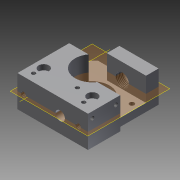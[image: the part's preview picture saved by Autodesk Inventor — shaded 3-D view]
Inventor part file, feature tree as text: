
AUTODESK INVENTOR PART (.ipt)
format: ipt  version: 2015 (Build 190159000, 159)  size: 257,536 bytes
history: native  units: mm
features: hole x11, extrude x4, projected_geometry x3, other x2, chamfer x1, plane x1, sketch x1
ambient origin geometry x8: Origin, YZ Plane, XZ Plane, XY Plane, X Axis, Y Axis, Z Axis, Center Point
bodies: Solid1 (feature_tree)
feature tree (23):
  extrude  "Extrusión1"  Depth=10.0mm
  hole  "Agujero1"  [1 undecoded]
  extrude  "Extrusión2"  Depth=10.0mm
  hole  "Agujero2"  [1 undecoded]
  hole  "Agujero3"  [1 undecoded]
  hole  "Agujero4"  [1 undecoded]
  hole  "Agujero5"  [1 undecoded]
  hole  "Agujero10"  [1 undecoded]
  hole  "Agujero11"  [1 undecoded]
  other  "Desplazar cara3"
  other  "Eje de trabajo1"
  hole  "Agujero13"  [1 undecoded]
  extrude  "Extrusión9"  Depth=10.0mm
  extrude  "Extrusión10"  Depth=10.0mm
  chamfer  "Chaflán4"  Distance=32.0mm
  hole  "Agujero14"  [1 undecoded]
  plane  "Plano de trabajo2"
  hole  "Agujero15"  [1 undecoded]
  hole  "Agujero16"  [1 undecoded]
  sketch  "Boceto15"  dims[d0=42.5mm d1=49.0mm d2=22.0mm d3=26.5mm d4=31.0mm d5=3.5mm d6=20.0mm d7=0.0mm d8=35.0mm d9=3.242mm d10=6.0mm d11=4.0mm d12=2.0mm d13=90.0deg d14=8.0mm d15=20.594885mm d17=13.0mm d19=15.0mm d20=0.0mm d22=6.0mm d23=6.0mm d24=6.0mm d25=4.0mm d26=2.0mm d27=90.0deg d28=20.0mm d29=20.594885mm d37=5.0mm d38=15.0mm d39=6.0mm d40=15.0mm d41=90.0deg d42=28.5mm d43=0.0mm d46=6.5mm d48=4.0mm d49=3.0mm d50=6.0mm d51=6.0mm d52=15.0mm d53=90.0deg d54=32.0mm d55=20.594885mm d58=8.566mm d59=6.0mm d60=6.0mm d61=15.0mm d62=90.0deg d63=15.0mm d64=20.594885mm d123=3.4mm d124=6.0mm d125=6.5mm d126=3.4mm d127=14.3117mm d128=8.0mm d129=20.594885mm d130=32.0mm d131=5.0mm d132=2.459mm d133=6.0mm d134=6.5mm d135=3.4mm d136=14.3117mm d137=6.0mm d138=20.594885mm d139=0.5mm d140=1.5mm d154=2.459mm d155=6.0mm d156=4.0mm d157=2.0mm d158=90.0deg d159=8.0mm d160=20.594885mm d161=6.0mm d162=25.0mm d163=10.0mm d164=0.0mm d168=2.5mm d169=0.0mm d170=4.0mm d171=2.0mm d172=45.0deg d173=4.0mm d174=15.0mm d175=2.459mm d176=6.0mm d177=4.0mm d178=2.0mm d179=90.0deg d180=6.0mm d181=20.594885mm d186=6.5mm d187=8.0mm d188=10.0mm d189=10.0mm d190=10.0mm d191=6.0mm d192=4.0mm d193=2.0mm d194=90.0deg d195=3.0mm d196=0.0mm d202=26.5mm d203=6.0mm d204=3.0mm d205=6.0mm d206=4.0mm d207=2.0mm d208=90.0deg d209=12.0mm d210=20.594885mm]
  projected_geometry  "Contorno proyectado1"
  projected_geometry  "Contorno proyectado2"
  projected_geometry  "Contorno proyectado3"
note: 11 required parameter values undecoded (feature->parameter linkage not recoverable at this tier; creation-order binding heuristic only, values carry confidence <= 0.55)
